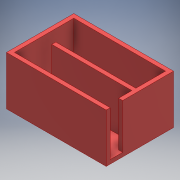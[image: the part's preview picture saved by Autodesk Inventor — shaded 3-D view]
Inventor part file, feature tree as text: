
AUTODESK INVENTOR PART (.ipt)
format: ipt  version: 2018 (Build 220112000, 112)  size: 144,896 bytes
history: native  units: mm
features: extrude x4, sketch x4, projected_geometry x4
ambient origin geometry x8: Origin, YZ Plane, XZ Plane, XY Plane, X Axis, Y Axis, Z Axis, Center Point
bodies: Solid1 (feature_tree)
feature tree (12):
  extrude  "Extrusion1"  Depth=270.0mm
  extrude  "Extrusion2"  Depth=16.0mm
  extrude  "Extrusion3"  Depth=16.0mm
  extrude  "Extrusion4"  Depth=180.0mm TaperAngle=0.0deg
  sketch  "Sketch1"  dims[d0=400.0mm d1=270.0mm]
  sketch  "Sketch2"  dims[d2=16.0mm d3=0.0mm d4=16.0mm]
  projected_geometry  "Projected Loop1"
  sketch  "Sketch3"  dims[d5=16.0mm d6=16.0mm]
  projected_geometry  "Projected Loop2"
  sketch  "Sketch4"  dims[d7=16.0mm d8=180.0mm d9=0.0mm d10=50.0mm d11=180.0mm d12=0.0mm d13=135.0mm d14=16.0mm d15=180.0mm d16=0.0mm]
  projected_geometry  "Projected Loop3"
  projected_geometry  "Projected Loop4"
